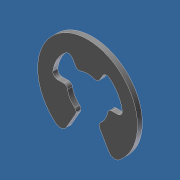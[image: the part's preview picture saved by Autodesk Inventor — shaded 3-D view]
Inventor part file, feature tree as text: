
AUTODESK INVENTOR PART (.ipt)
format: ipt  version: unknown  size: 201,728 bytes
history: native  units: in
note: dims shown in document units (in); Inventor stores cm internally (conversion verified against a paired STEP export)
features: other x7, extrude x1, sketch x1
ambient origin geometry x8: Origin, YZ Plane, XZ Plane, XY Plane, X Axis, Y Axis, Z Axis, Center Point
feature tree (9):
  extrude  "Extrusion1"  [1 undecoded]
  other  "RR_XY"
  other  "RR_YZ"
  other  "RR_ZX"
  other  "RR_X"
  other  "RR_Y"
  other  "RR_Z"
  other  "RR_Center"
  sketch  "Sketch_1"  dims[d0=0.0365in d1=0.0in]
note: 1 required parameter value undecoded (feature->parameter linkage not recoverable at this tier; creation-order binding heuristic only, values carry confidence <= 0.55)
